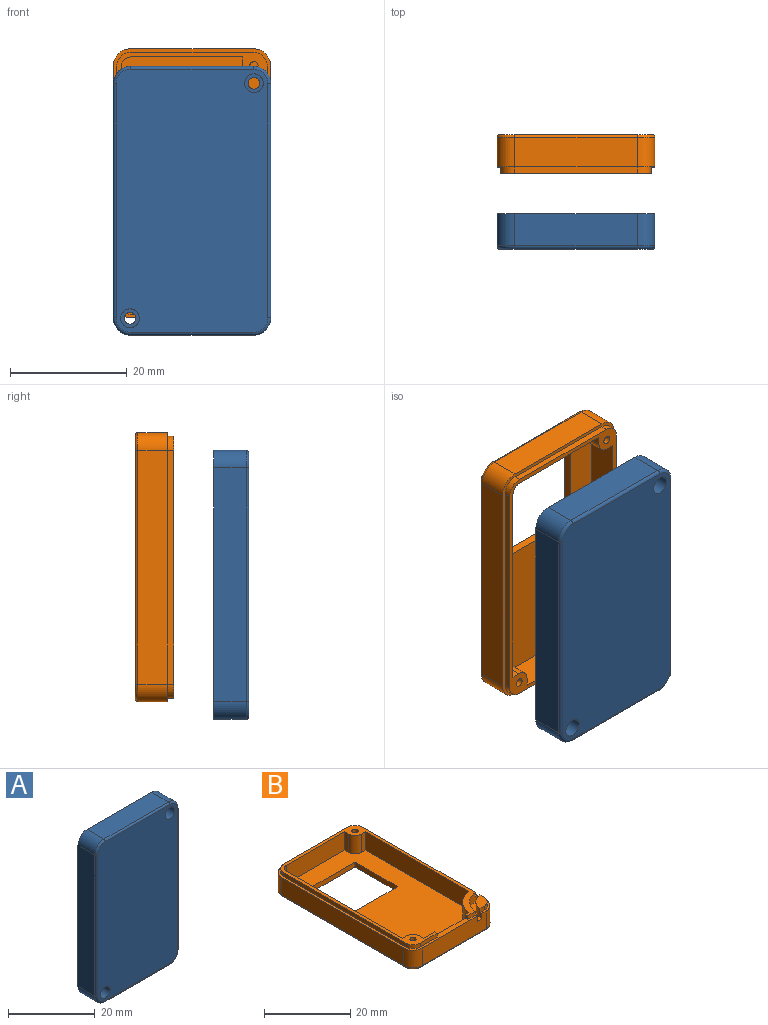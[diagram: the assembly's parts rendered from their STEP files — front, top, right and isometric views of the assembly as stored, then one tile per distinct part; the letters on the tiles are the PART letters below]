
ASSEMBLY  parts=2 mates=1
PART A: 47 faces, bbox 27.5x6x46.5 mm
  f0: plane 45x26mm, normal (0,-1,0), area 1148.5mm2, adj f1,f23,f24,f25,f26,f27,f28,f29
  f1: cylinder r=1.6mm len=4.2mm, axis (0,-1,0), area 42.2mm2, adj f0,f2
  f2: plane 3.2x3.2mm, normal (0,-1,0), area 4.9mm2, adj f1,f45
  f3: plane 3.2x3.2mm, normal (0,-1,0), area 4.9mm2, adj f4,f46
  f4: cylinder r=1mm len=2mm, axis (0,1,0), area 7.5mm2, adj f3,f5
  f5: plane 45.1x26.1mm, normal (0,1,0), area 155.7mm2, adj f4,f6,f7,f8,f11,f12,f13,f14
  f6: plane 15.42x4mm, normal (0,0,1), area 61.7mm2, adj f5,f8,f9,f17
  f7: plane 4x2.83mm, normal (0,0,1), area 11.3mm2, adj f5,f10,f18,f19
  f8: cylinder r=6.7mm len=5.15mm, axis (0,1,0), area 30.8mm2, adj f5,f6,f9,f11
  f9: plane 43.2x24.2mm, normal (0,1,0), area 996.5mm2, adj f6,f8,f11,f13,f14,f15,f16,f17
  f10: plane 4.43x4.43mm, normal (0,1,0), area 13mm2, adj f7,f12,f18,f19
  f11: plane 34.42x4mm, normal (-1,0,0), area 137.7mm2, adj f5,f8,f9,f13
  f12: plane 4x2.83mm, normal (-1,0,0), area 11.3mm2, adj f5,f10,f18,f19
  f13: cylinder r=2.6mm len=4.1mm, axis (0,1,0), area 29.1mm2, adj f5,f9,f11,f14
  f14: plane 18.98x4mm, normal (0,0,-1), area 75.9mm2, adj f5,f9,f13,f15
  f15: cylinder r=1.6mm len=4mm, axis (0,-1,0), area 10.1mm2, adj f5,f9,f14,f16
  f16: plane 37.98x4mm, normal (1,0,0), area 151.9mm2, adj f5,f9,f15,f17
  f17: cylinder r=2.6mm len=4.1mm, axis (0,1,0), area 29.1mm2, adj f5,f6,f9,f16
  f18: cylinder r=6mm len=4.43mm, axis (0,1,0), area 26.4mm2, adj f5,f7,f10,f12
  f19: cylinder r=1.6mm len=4mm, axis (0,-1,0), area 10.1mm2, adj f5,f7,f10,f12
  f20: plane 40x0.6mm, normal (-1,0,0), area 24mm2, adj f5,f21,f38,f44
  f21: plane 46x27mm, normal (0,1,0), area 62.7mm2, adj f20,f22,f31,f32,f33,f34,f35,f36
  f22: cylinder r=3mm len=5.5mm, axis (0,-1,0), area 25.9mm2, adj f21,f23,f31,f37
  f23: torus R=2.5mm, axis (0,-1,0), area 3.5mm2, adj f0,f22,f24,f30
  f24: cylinder r=0.5mm len=21mm, axis (-1,0,0), area 16.5mm2, adj f0,f23,f25,f37
  f25: torus R=2.5mm, axis (0,-1,0), area 3.5mm2, adj f0,f24,f26,f36
  f26: cylinder r=0.5mm len=40mm, axis (0,0,-1), area 31.4mm2, adj f0,f25,f27,f35
  f27: torus R=2.5mm, axis (0,-1,0), area 3.5mm2, adj f0,f26,f28,f34
  f28: cylinder r=0.5mm len=21mm, axis (1,0,0), area 16.5mm2, adj f0,f27,f29,f33
  f29: torus R=2.5mm, axis (0,-1,0), area 3.5mm2, adj f0,f28,f30,f32
  f30: cylinder r=0.5mm len=40mm, axis (0,0,1), area 31.4mm2, adj f0,f23,f29,f31
  f31: plane 40x5.5mm, normal (1,0,0), area 220mm2, adj f21,f22,f30,f32
  f32: cylinder r=3mm len=5.5mm, axis (0,-1,0), area 25.9mm2, adj f21,f29,f31,f33
  f33: plane 21x5.5mm, normal (0,0,-1), area 115.5mm2, adj f21,f28,f32,f34
  f34: cylinder r=3mm len=5.5mm, axis (0,-1,0), area 25.9mm2, adj f21,f27,f33,f35
  f35: plane 40x5.5mm, normal (-1,0,0), area 220mm2, adj f21,f26,f34,f36
  f36: cylinder r=3mm len=5.5mm, axis (0,-1,0), area 25.9mm2, adj f21,f25,f35,f37
  f37: plane 21x5.5mm, normal (0,0,1), area 115.5mm2, adj f21,f22,f24,f36
  f38: cylinder r=2.55mm len=2.55mm, axis (0,1,0), area 2.4mm2, adj f5,f20,f21,f39
  f39: plane 21x0.6mm, normal (0,0,1), area 12.6mm2, adj f5,f21,f38,f40
  f40: cylinder r=2.55mm len=2.55mm, axis (0,1,0), area 2.4mm2, adj f5,f21,f39,f41
  f41: plane 40x0.6mm, normal (1,0,0), area 24mm2, adj f5,f21,f40,f42
  f42: cylinder r=2.55mm len=2.55mm, axis (0,1,0), area 2.4mm2, adj f5,f21,f41,f43
  f43: plane 21x0.6mm, normal (0,0,-1), area 12.6mm2, adj f5,f21,f42,f44
  f44: cylinder r=2.55mm len=2.55mm, axis (0,1,0), area 2.4mm2, adj f5,f20,f21,f43
  f45: cylinder r=1mm len=2mm, axis (0,1,0), area 7.5mm2, adj f2,f5
  f46: cylinder r=1.6mm len=4.2mm, axis (0,-1,0), area 42.2mm2, adj f0,f3
PART B: 67 faces, bbox 27.5x46.5x6.6 mm
  f0: plane 3.86x3.86mm, normal (0,0,1), area 9.6mm2, adj f55,f56,f57,f58
  f1: plane 44.84x25.84mm, normal (0,0,1), area 121.7mm2, adj f2,f3,f8,f9,f30,f31,f32,f33
  f2: cylinder r=6mm len=6mm, axis (0,0,-1), area 23.2mm2, adj f1,f4,f28,f29,f43,f59,f66
  f3: plane 1.1x0.8mm, normal (-1,0,0), area 0.9mm2, adj f1,f29,f31,f66
  f4: plane 6x6mm, normal (0,0,1), area 12.4mm2, adj f2,f28,f43,f55
  f5: plane 1.4x1.4mm, normal (0,0,1), area 1.5mm2, adj f8
  f6: plane 1.4x1.4mm, normal (0,0,1), area 1.5mm2, adj f9
  f7: plane 43.2x24.2mm, normal (0,0,1), area 801.8mm2, adj f14,f15,f16,f17,f18,f19,f20,f21
  f8: cylinder r=0.7mm len=5.2mm, axis (0,0,1), area 22.9mm2, adj f1,f5
  f9: cylinder r=0.7mm len=5.2mm, axis (0,0,1), area 22.9mm2, adj f1,f6
  f10: plane 4.5x4.5mm, normal (0,0,1), area 4.3mm2, adj f11,f28,f43,f55,f56,f57,f58
  f11: cylinder r=3mm len=5mm, axis (0,0,1), area 23.6mm2, adj f10,f12,f28,f43
  f12: torus R=2.5mm, axis (0,0,1), area 3.5mm2, adj f11,f13,f27,f44
  f13: plane 45x26mm, normal (0,0,-1), area 590.7mm2, adj f12,f14,f15,f16,f17,f18,f19,f20
  f14: plane 13.6x1.4mm, normal (-1,0,0), area 19mm2, adj f7,f13,f15,f21
  f15: cylinder r=0.2mm len=1.4mm, axis (0,0,-1), area 0.4mm2, adj f7,f13,f14,f16
  f16: plane 13.6x1.4mm, normal (0,-1,0), area 19mm2, adj f7,f13,f15,f17
  f17: cylinder r=0.2mm len=1.4mm, axis (0,0,-1), area 0.4mm2, adj f7,f13,f16,f18
  f18: plane 13.6x1.4mm, normal (1,0,0), area 19mm2, adj f7,f13,f17,f19
  f19: cylinder r=0.2mm len=1.4mm, axis (0,0,-1), area 0.4mm2, adj f7,f13,f18,f20
  f20: plane 13.6x1.4mm, normal (0,1,0), area 19mm2, adj f7,f13,f19,f21
  f21: cylinder r=0.2mm len=1.4mm, axis (0,0,-1), area 0.4mm2, adj f7,f13,f14,f20
  f22: plane 18x0.2mm, normal (1,0,0), area 3.6mm2, adj f13,f23,f25,f26
  f23: plane 21x0.2mm, normal (0,1,0), area 4.2mm2, adj f13,f22,f24,f26
  f24: plane 18x0.2mm, normal (-1,0,0), area 3.6mm2, adj f13,f23,f25,f26
  f25: plane 21x0.2mm, normal (0,-1,0), area 4.2mm2, adj f13,f22,f24,f26
  f26: plane 21x18mm, normal (0,0,-1), area 378mm2, adj f22,f23,f24,f25
  f27: cylinder r=0.5mm len=40mm, axis (0,-1,0), area 31.4mm2, adj f12,f13,f28,f49
  f28: plane 40x5mm, normal (1,0,0), area 197.8mm2, adj f2,f4,f10,f11,f27,f29,f50,f55
  f29: plane 46.02x27.02mm, normal (0,0,1), area 85mm2, adj f2,f3,f28,f30,f31,f43,f50,f51
  f30: plane 1.1x0.8mm, normal (1,0,0), area 0.9mm2, adj f1,f29,f31,f65
  f31: plane 14.8x5.2mm, normal (0,1,0), area 66mm2, adj f1,f3,f7,f29,f30,f32,f42
  f32: plane 5.2x1.4mm, normal (1,0,0), area 7.3mm2, adj f1,f7,f31,f33
  f33: cylinder r=2mm len=5.2mm, axis (0,0,-1), area 16.3mm2, adj f1,f7,f32,f34
  f34: plane 5.2x1.4mm, normal (0,1,0), area 7.3mm2, adj f1,f7,f33,f35
  f35: plane 38.2x5.2mm, normal (1,0,0), area 198.6mm2, adj f1,f7,f34,f36
  f36: cylinder r=1.6mm len=5.2mm, axis (0,0,-1), area 13.1mm2, adj f1,f7,f35,f37
  f37: plane 19.2x5.2mm, normal (0,-1,0), area 99.8mm2, adj f1,f7,f36,f38
  f38: plane 5.2x1.4mm, normal (-1,0,0), area 7.3mm2, adj f1,f7,f37,f39
  f39: cylinder r=2mm len=5.2mm, axis (0,0,-1), area 16.3mm2, adj f1,f7,f38,f40
  f40: plane 5.2x1.4mm, normal (0,-1,0), area 7.3mm2, adj f1,f7,f39,f41
  f41: plane 33.8x5.2mm, normal (-1,0,0), area 175.8mm2, adj f1,f7,f40,f42
  f42: cylinder r=7.4mm len=6mm, axis (0,0,-1), area 47mm2, adj f1,f7,f31,f41
  f43: plane 21x5mm, normal (0,-1,0), area 102.8mm2, adj f2,f4,f10,f11,f29,f44,f54,f55
  f44: cylinder r=0.5mm len=21mm, axis (-1,0,0), area 16.5mm2, adj f12,f13,f43,f45
  f45: torus R=2.5mm, axis (0,0,1), area 3.5mm2, adj f13,f44,f46,f54
  f46: cylinder r=0.5mm len=40mm, axis (0,1,0), area 31.4mm2, adj f13,f45,f47,f53
  f47: torus R=2.5mm, axis (0,0,1), area 3.5mm2, adj f13,f46,f48,f52
  f48: cylinder r=0.5mm len=21mm, axis (1,0,0), area 16.5mm2, adj f13,f47,f49,f51
  f49: torus R=2.5mm, axis (0,0,-1), area 3.5mm2, adj f13,f27,f48,f50
  f50: cylinder r=3mm len=5mm, axis (0,0,-1), area 23.6mm2, adj f28,f29,f49,f51
  f51: plane 21x5mm, normal (0,1,0), area 105mm2, adj f29,f48,f50,f52
  f52: cylinder r=3mm len=5mm, axis (0,0,1), area 23.6mm2, adj f29,f47,f51,f53
  f53: plane 40x5mm, normal (-1,0,0), area 200mm2, adj f29,f46,f52,f54
  f54: cylinder r=3mm len=5mm, axis (0,0,1), area 23.6mm2, adj f29,f43,f45,f53
  f55: cylinder r=4.5mm len=4.5mm, axis (0,0,-1), area 17.1mm2, adj f0,f4,f10,f28,f43,f56,f57
  f56: plane 1.46x1.1mm, normal (1,0,0), area 1.6mm2, adj f0,f10,f55,f58
  f57: plane 1.46x1.1mm, normal (0,-1,0), area 1.6mm2, adj f0,f10,f55,f58
  f58: cylinder r=2.4mm len=2.4mm, axis (0,0,1), area 4.1mm2, adj f0,f10,f56,f57
  f59: plane 37.04x1.12mm, normal (1,0,0), area 40.7mm2, adj f1,f2,f29,f60
  f60: cylinder r=2.4mm len=2.4mm, axis (0,0,1), area 4.1mm2, adj f1,f29,f59,f61
  f61: plane 21x1.1mm, normal (0,1,0), area 23.1mm2, adj f1,f29,f60,f62
  f62: cylinder r=2.4mm len=2.4mm, axis (0,0,1), area 4.1mm2, adj f1,f29,f61,f63
  f63: plane 40x1.1mm, normal (-1,0,0), area 44mm2, adj f1,f29,f62,f64
  f64: cylinder r=2.4mm len=2.4mm, axis (0,0,1), area 4.1mm2, adj f1,f29,f63,f65
  f65: plane 5.5x1.1mm, normal (0,-1,0), area 6mm2, adj f1,f29,f30,f64
  f66: plane 2.54x1.12mm, normal (0,-1,0), area 2.8mm2, adj f1,f2,f3,f29
PLACE A t=(-0.17,2.03,9.84)mm
PLACE B rot(axis=(1,0,0),90deg) t=(-0.17,-10.47,-20.56)mm
MATE parallel B.f10 <-> A.f21  axis (0,1,0) through (13.33,16.03,-16.66)mm
